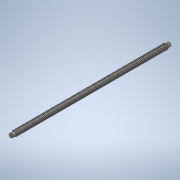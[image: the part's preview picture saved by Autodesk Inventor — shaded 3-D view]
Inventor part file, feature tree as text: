
AUTODESK INVENTOR PART (.ipt)
format: ipt  version: 2020 (Build 240168000, 168)  size: 882,176 bytes
history: native  units: mm
features: sketch x7, extrude x6, other x3, chamfer x2
ambient origin geometry x8: Origin, YZ Plane, XZ Plane, XY Plane, X Axis, Y Axis, Z Axis, Center Point
bodies: Body1 (feature_tree)
feature tree (18):
  other  "Bryła1"
  extrude  "Wyciągnięcie proste1"  Depth=13.64mm
  other  "Zwój1"
  extrude  "Wyciągnięcie proste2"  Depth=487.5mm TaperAngle=0.0deg
  extrude  "Wyciągnięcie proste3"  TaperAngle=120.0deg  [1 undecoded]
  extrude  "Wyciągnięcie proste4"  TaperAngle=120.0deg  [1 undecoded]
  other  "Płaszczyzna konstrukcyjna1"
  extrude  "Wyciągnięcie proste5"  Depth=8.0mm
  chamfer  "Faza1"  Distance=1.0mm
  extrude  "Wyciągnięcie proste6"  Depth=20.0mm
  chamfer  "Faza2"  Distance=12.0mm
  sketch  "Szkic1"
  sketch  "Szkic2"
  sketch  "Szkic3"
  sketch  "Szkic4"
  sketch  "Szkic5"
  sketch  "Szkic7"
  sketch  "Szkic8"
note: 2 required parameter values undecoded (feature->parameter linkage not recoverable at this tier; creation-order binding heuristic only, values carry confidence <= 0.55)
